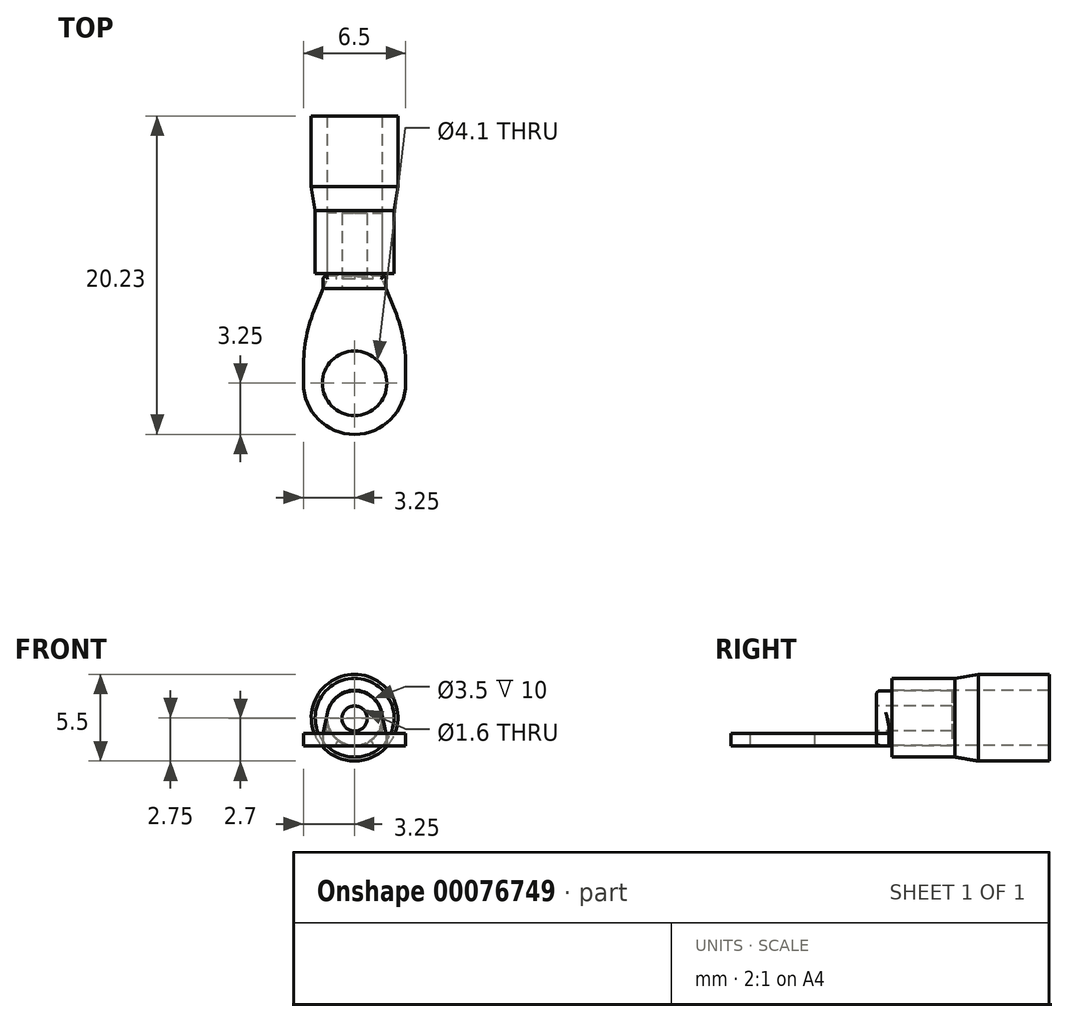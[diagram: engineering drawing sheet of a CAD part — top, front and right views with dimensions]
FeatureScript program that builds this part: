
annotation { "Feature Type Name" : "Feature", "Feature Type Description" : "" }
export const myFeature = defineFeature(function(context is Context, id is Id, definition is map)
    precondition{}
    {
        {
            var Q0;
            Q0=qCreatedBy(makeId("Top.planeOp"),FACE);
            var sketch = newSketch(context, id + "F0", { "sketchPlane" : qUnion([Q0])});
            skLineSegment(sketch, "E0.bottom", {"start": v(2, 4.52) * mm, "end": v(-2, 4.52) * mm});
            skLineSegment(sketch, "E0.left", {"start": v(3.25, -0.48) * mm, "end": v(3.25, -1.48) * mm});
            skLineSegment(sketch, "E0.right", {"start": v(-3.25, -0.48) * mm, "end": v(-3.25, -1.48) * mm});
            skLineSegment(sketch, "E1", {"start": v(-2.48, 3.37) * mm, "end": v(-2, 4.52) * mm});
            skLineSegment(sketch, "E2", {"start": v(2.48, 3.37) * mm, "end": v(2, 4.52) * mm});
            skLineSegment(sketch, "E3", {"start": v(0, -4.48) * mm, "end": v(0, 4.52) * mm, "construction": true});
            skPoint(sketch, "E4.visualSharp", {"position": v(-3.25, 1.52) * mm});
            skArc(sketch, "E4.filletArc", {"start": v(-2.48, 3.37) * mm, "mid": v(-3.06, 1.48) * mm, "end": v(-3.25, -0.48) * mm});
            skPoint(sketch, "E5.visualSharp", {"position": v(3.25, 1.52) * mm});
            skArc(sketch, "E5.filletArc", {"start": v(3.25, -0.48) * mm, "mid": v(3.06, 1.48) * mm, "end": v(2.48, 3.37) * mm});
            skCircle(sketch, "E6", {"center": v(0, -1.48) * mm, "radius": 2.05 * mm});
            skArc(sketch, "E7", {"start": v(-3.25, -1.48) * mm, "mid": v(0, -4.73) * mm, "end": v(3.25, -1.48) * mm});
            skPoint(sketch, "E8.end.orphan", {"position": v(-2.05, -1.48) * mm});
            skPoint(sketch, "E9.orphan", {"position": v(2.05, -1.48) * mm});
            skSolve(sketch);
        }
        {
            var Q0;
            Q0=qSketchRegion(id+"F0",true);
            extrude(context, id + "F1", {"entities" : qUnion([Q0]), "depth" : 0.8 * mm});
        }
        {
            var Q0;
            Q0=makeQuery(id+"F1.opExtrude","SWEPT_FACE",FACE,{"disambiguationData":[OSD([sQuery(id+"F0.wireOp",EDGE,"E0.bottom")])]});
            var sketch = newSketch(context, id + "F2", { "sketchPlane" : qUnion([Q0])});
            skCircle(sketch, "E10", {"center": v(0, 1.75) * mm, "radius": 0.8 * mm});
            skArc(sketch, "E11", {"start": v(1.7, 2.12) * mm, "mid": v(0, 3.5) * mm, "end": v(-1.7, 2.12) * mm});
            skLineSegment(sketch, "E12", {"start": v(-2, 0) * mm, "end": v(-2, 0.8) * mm});
            skLineSegment(sketch, "E13", {"start": v(-2, 0.8) * mm, "end": v(-1.7, 2.12) * mm});
            skLineSegment(sketch, "E14", {"start": v(2, 0) * mm, "end": v(2, 0.8) * mm});
            skLineSegment(sketch, "E15", {"start": v(2, 0.8) * mm, "end": v(1.7, 2.12) * mm});
            skLineSegment(sketch, "E16", {"start": v(-2, 0) * mm, "end": v(2, 0) * mm});
            skSolve(sketch);
        }
        {
            var Q0;
            Q0=qSketchRegion(id+"F2",true);
            extrude(context, id + "F3", {"entities" : qUnion([Q0]), "operationType" : NewBodyOperationType.ADD, "depth" : 0.8 * mm});
        }
        {
            var Q0;
            Q0=makeQuery(id+"F3.opExtrude","CAP_FACE",FACE,{"disambiguationData":[OSD([sQuery(id+"F2.wireOp",EDGE,"E10"),sQuery(id+"F2.wireOp",EDGE,"E11"),sQuery(id+"F2.wireOp",EDGE,"E12"),sQuery(id+"F2.wireOp",EDGE,"E13"),sQuery(id+"F2.wireOp",EDGE,"E14"),sQuery(id+"F2.wireOp",EDGE,"E15"),sQuery(id+"F2.wireOp",EDGE,"E16")])],"isStart":false});
            var sketch = newSketch(context, id + "F4", { "sketchPlane" : qUnion([Q0])});
            skCircle(sketch, "E17", {"center": v(0, 1.75) * mm, "radius": 1.75 * mm});
            skCircle(sketch, "E18", {"center": v(0, 1.75) * mm, "radius": 0.8 * mm});
            skSolve(sketch);
        }
        {
            var Q0;
            Q0=qSketchRegion(id+"F4",true);
            extrude(context, id + "F5", {"entities" : qUnion([Q0]), "operationType" : NewBodyOperationType.ADD, "depth" : 4 * mm});
        }
        {
            var Q0;
            {var subQ0=sQuery(id+"F2.wireOp",EDGE,"E13");var subQ3=sQuery(id+"F4.wireOp",EDGE,"E17");Q0=makeQuery(id+"F5.boolean.opBoolean","SPLIT",EDGE,{"disambiguationData":[TD([makeQuery(id+"F3.opExtrude","SWEPT_FACE",FACE,{"disambiguationData":[OSD([subQ0])]})])],"derivedFrom":makeQuery(id+"F5.opExtrude","CAP_EDGE",EDGE,{"disambiguationData":[OSD([subQ3])],"isStart":true})});}
            var Q1;
            {var subQ0=sQuery(id+"F2.wireOp",EDGE,"E15");var subQ3=sQuery(id+"F4.wireOp",EDGE,"E17");Q1=makeQuery(id+"F5.boolean.opBoolean","SPLIT",EDGE,{"disambiguationData":[TD([makeQuery(id+"F3.opExtrude","SWEPT_FACE",FACE,{"disambiguationData":[OSD([subQ0])]})])],"derivedFrom":makeQuery(id+"F5.opExtrude","CAP_EDGE",EDGE,{"disambiguationData":[OSD([subQ3])],"isStart":true})});}
            var Q2;
            Q2=makeQuery(id+"F3.opExtrude","CAP_EDGE",EDGE,{"disambiguationData":[OSD([sQuery(id+"F2.wireOp",EDGE,"E14")])],"isStart":false});
            var Q3;
            {var subQ0=sQuery(id+"F2.wireOp",EDGE,"E14");var subQ2=sQuery(id+"F2.wireOp",EDGE,"E16");Q3=makeQuery(id+"F5.boolean.opBoolean","SPLIT",EDGE,{"disambiguationData":[TD([makeQuery(id+"F3.opExtrude","SWEPT_FACE",FACE,{"disambiguationData":[OSD([subQ0])]})])],"derivedFrom":makeQuery(id+"F3.opExtrude","CAP_EDGE",EDGE,{"disambiguationData":[OSD([subQ2])],"isStart":false})});}
            var Q4;
            {var subQ0=sQuery(id+"F2.wireOp",EDGE,"E12");var subQ2=sQuery(id+"F2.wireOp",EDGE,"E16");Q4=makeQuery(id+"F5.boolean.opBoolean","SPLIT",EDGE,{"disambiguationData":[TD([makeQuery(id+"F3.opExtrude","SWEPT_FACE",FACE,{"disambiguationData":[OSD([subQ0])]})])],"derivedFrom":makeQuery(id+"F3.opExtrude","CAP_EDGE",EDGE,{"disambiguationData":[OSD([subQ2])],"isStart":false})});}
            var Q5;
            Q5=makeQuery(id+"F3.opExtrude","CAP_EDGE",EDGE,{"disambiguationData":[OSD([sQuery(id+"F2.wireOp",EDGE,"E12")])],"isStart":false});
            var Q6;
            Q6=makeQuery(id+"F3.opExtrude","CAP_EDGE",EDGE,{"disambiguationData":[OSD([sQuery(id+"F2.wireOp",EDGE,"E13")])],"isStart":false});
            var Q7;
            Q7=makeQuery(id+"F3.opExtrude","CAP_EDGE",EDGE,{"disambiguationData":[OSD([sQuery(id+"F2.wireOp",EDGE,"E15")])],"isStart":false});
            var Q8;
            Q8=makeQuery(id+"F3.opExtrude","SWEPT_EDGE",EDGE,{"disambiguationData":[OSD([sQuery(id+"F2.wireOp",EDGE,"E14"),sQuery(id+"F2.wireOp",EDGE,"E16")])]});
            var Q9;
            Q9=makeQuery(id+"F3.opExtrude","SWEPT_EDGE",EDGE,{"disambiguationData":[OSD([sQuery(id+"F2.wireOp",EDGE,"E12"),sQuery(id+"F2.wireOp",EDGE,"E16")])]});
            var Q10;
            Q10=makeQuery(id+"F3.opExtrude","CAP_EDGE",EDGE,{"disambiguationData":[OSD([sQuery(id+"F2.wireOp",EDGE,"E13")])],"isStart":true});
            var Q11;
            Q11=makeQuery(id+"F3.opExtrude","CAP_EDGE",EDGE,{"disambiguationData":[OSD([sQuery(id+"F2.wireOp",EDGE,"E11")])],"isStart":true});
            fillet(context, id + "F6", {"entities" : qUnion([Q0, Q1, Q2, Q3, Q4, Q5, Q6, Q7, Q8, Q9, Q10, Q11]), "radius" : 0.2 * mm, "tangentPropagation" : true, "allowEdgeOverflow" : false});
        }
        {
            var Q0;
            Q0=makeQuery(id+"F1.opExtrude","CAP_FACE",FACE,{"disambiguationData":[OSD([sQuery(id+"F0.wireOp",EDGE,"E0.bottom"),sQuery(id+"F0.wireOp",EDGE,"E0.top"),sQuery(id+"F0.wireOp",EDGE,"E0.left"),sQuery(id+"F0.wireOp",EDGE,"E0.right"),sQuery(id+"F0.wireOp",EDGE,"ZH0r6PSV-zSQv-AgWN-nJVd-TW3JIgmWmYPy"),sQuery(id+"F0.wireOp",EDGE,"E8"),sQuery(id+"F0.wireOp",EDGE,"8b582a4d-1064-4827-9666-be3c81ff932b"),sQuery(id+"F0.wireOp",EDGE,"E1"),sQuery(id+"F0.wireOp",EDGE,"E2"),sQuery(id+"F0.wireOp",EDGE,"0d03979d-8958-47e8-9159-c9e161dbd41a.trimOffspring"),sQuery(id+"F0.wireOp",EDGE,"E4.filletArc"),sQuery(id+"F0.wireOp",EDGE,"E5.filletArc")])],"isStart":false});
            cPlane(context, id + "F7", {"entities" : qUnion([Q0]), "cplaneType" : CPlaneType.OFFSET, "offset" : 1 * mm, "width" : 150 * mm, "height" : 150 * mm});
        }
        {
            var Q0;
            Q0=qCreatedBy(id+"F7.planeOp",FACE);
            var sketch = newSketch(context, id + "F8", { "sketchPlane" : qUnion([Q0])});
            skLineSegment(sketch, "E19", {"start": v(0, 5.5) * mm, "end": v(0, 15.5) * mm, "construction": true});
            skLineSegment(sketch, "E20", {"start": v(-1.75, 5.5) * mm, "end": v(-1.75, 15.5) * mm});
            skLineSegment(sketch, "E21", {"start": v(-1.75, 15.5) * mm, "end": v(-2.75, 15.5) * mm});
            skLineSegment(sketch, "E22", {"start": v(-2.75, 15.5) * mm, "end": v(-2.75, 11) * mm});
            skLineSegment(sketch, "E23", {"start": v(-2.5, 9.5) * mm, "end": v(-2.5, 5.5) * mm});
            skLineSegment(sketch, "E24", {"start": v(-2.5, 5.5) * mm, "end": v(-1.75, 5.5) * mm});
            skLineSegment(sketch, "E25", {"start": v(-2.75, 11) * mm, "end": v(-2.5, 9.5) * mm});
            skSolve(sketch);
        }
        {
            var Q0;
            Q0=qSketchRegion(id+"F8",true);
            var Q1;
            Q1=sQuery(id+"F8.wireOp",EDGE,"E19");
            revolve(context, id + "F9", {"entities" : qUnion([Q0]), "axis" : qUnion([Q1]), "revolveType" : RevolveType.FULL});
        }
    });
